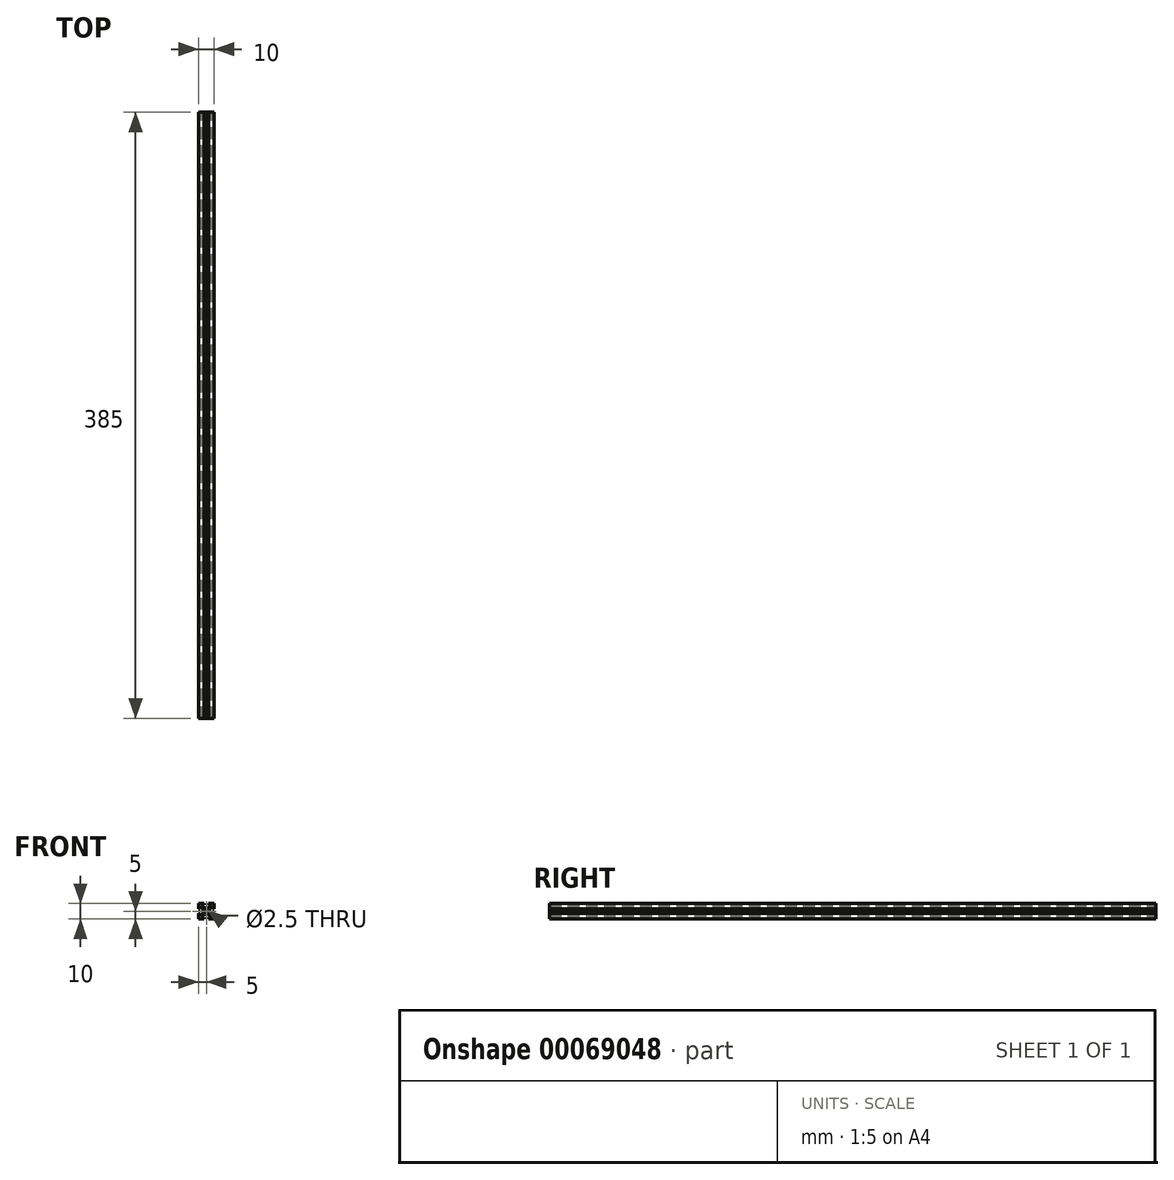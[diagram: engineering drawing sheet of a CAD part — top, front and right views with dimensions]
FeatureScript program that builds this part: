
annotation { "Feature Type Name" : "Feature", "Feature Type Description" : "" }
export const myFeature = defineFeature(function(context is Context, id is Id, definition is map)
    precondition{}
    {
        {
            var Q0;
            Q0=qCreatedBy(makeId("Front.planeOp"),FACE);
            var sketch = newSketch(context, id + "F0", { "sketchPlane" : qUnion([Q0])});
            skLineSegment(sketch, "E0", {"start": v(0, 0) * mm, "end": v(0, 3.5) * mm});
            skLineSegment(sketch, "E1", {"start": v(0, 3.5) * mm, "end": v(-1, 3.5) * mm});
            skLineSegment(sketch, "E2", {"start": v(-1, 3.5) * mm, "end": v(-1, 2) * mm});
            skLineSegment(sketch, "E3", {"start": v(-1, 2) * mm, "end": v(-3, 4) * mm});
            skLineSegment(sketch, "E4", {"start": v(-3, 4) * mm, "end": v(-3, 5) * mm});
            skLineSegment(sketch, "E5", {"start": v(-3, 5) * mm, "end": v(-5, 5) * mm, "construction": true});
            skLineSegment(sketch, "E6", {"start": v(-5, 5) * mm, "end": v(0, 0) * mm, "construction": true});
            skLineSegment(sketch, "E7.MirrorCS", {"start": v(-3.5, 0) * mm, "end": v(-3.5, 1) * mm});
            skLineSegment(sketch, "E8.MirrorCS", {"start": v(0, 0) * mm, "end": v(-3.5, 0) * mm});
            skLineSegment(sketch, "E9.MirrorCS", {"start": v(-3.5, 1) * mm, "end": v(-2, 1) * mm});
            skLineSegment(sketch, "E10.MirrorCS", {"start": v(-2, 1) * mm, "end": v(-4, 3) * mm});
            skLineSegment(sketch, "E11.MirrorCS", {"start": v(-4, 3) * mm, "end": v(-5, 3) * mm});
            skLineSegment(sketch, "E12.MirrorCS", {"start": v(-5, 3) * mm, "end": v(-5, 5) * mm, "construction": true});
            skLineSegment(sketch, "E13.1.0", {"start": v(-3, 6) * mm, "end": v(-3, 5) * mm});
            skLineSegment(sketch, "E13.1.1", {"start": v(-1, 8) * mm, "end": v(-3, 6) * mm});
            skLineSegment(sketch, "E13.1.2", {"start": v(-1, 6.5) * mm, "end": v(-1, 8) * mm});
            skLineSegment(sketch, "E13.1.3", {"start": v(0, 6.5) * mm, "end": v(-1, 6.5) * mm});
            skLineSegment(sketch, "E13.1.4", {"start": v(0, 10) * mm, "end": v(0, 6.5) * mm});
            skLineSegment(sketch, "E13.1.5", {"start": v(0, 10) * mm, "end": v(-3.5, 10) * mm});
            skLineSegment(sketch, "E13.1.6", {"start": v(-3.5, 10) * mm, "end": v(-3.5, 9) * mm});
            skLineSegment(sketch, "E13.1.7", {"start": v(-3.5, 9) * mm, "end": v(-2, 9) * mm});
            skLineSegment(sketch, "E13.1.8", {"start": v(-2, 9) * mm, "end": v(-4, 7) * mm});
            skLineSegment(sketch, "E13.1.9", {"start": v(-4, 7) * mm, "end": v(-5, 7) * mm});
            skLineSegment(sketch, "E13.2.0", {"start": v(-6, 7) * mm, "end": v(-5, 7) * mm});
            skLineSegment(sketch, "E13.2.1", {"start": v(-8, 9) * mm, "end": v(-6, 7) * mm});
            skLineSegment(sketch, "E13.2.2", {"start": v(-6.5, 9) * mm, "end": v(-8, 9) * mm});
            skLineSegment(sketch, "E13.2.3", {"start": v(-6.5, 10) * mm, "end": v(-6.5, 9) * mm});
            skLineSegment(sketch, "E13.2.4", {"start": v(-10, 10) * mm, "end": v(-6.5, 10) * mm});
            skLineSegment(sketch, "E13.2.5", {"start": v(-10, 10) * mm, "end": v(-10, 6.5) * mm});
            skLineSegment(sketch, "E13.2.6", {"start": v(-10, 6.5) * mm, "end": v(-9, 6.5) * mm});
            skLineSegment(sketch, "E13.2.7", {"start": v(-9, 6.5) * mm, "end": v(-9, 8) * mm});
            skLineSegment(sketch, "E13.2.8", {"start": v(-9, 8) * mm, "end": v(-7, 6) * mm});
            skLineSegment(sketch, "E13.2.9", {"start": v(-7, 6) * mm, "end": v(-7, 5) * mm});
            skLineSegment(sketch, "E13.3.0", {"start": v(-7, 4) * mm, "end": v(-7, 5) * mm});
            skLineSegment(sketch, "E13.3.1", {"start": v(-9, 2) * mm, "end": v(-7, 4) * mm});
            skLineSegment(sketch, "E13.3.2", {"start": v(-9, 3.5) * mm, "end": v(-9, 2) * mm});
            skLineSegment(sketch, "E13.3.3", {"start": v(-10, 3.5) * mm, "end": v(-9, 3.5) * mm});
            skLineSegment(sketch, "E13.3.4", {"start": v(-10, 0) * mm, "end": v(-10, 3.5) * mm});
            skLineSegment(sketch, "E13.3.5", {"start": v(-10, 0) * mm, "end": v(-6.5, 0) * mm});
            skLineSegment(sketch, "E13.3.6", {"start": v(-6.5, 0) * mm, "end": v(-6.5, 1) * mm});
            skLineSegment(sketch, "E13.3.7", {"start": v(-6.5, 1) * mm, "end": v(-8, 1) * mm});
            skLineSegment(sketch, "E13.3.8", {"start": v(-8, 1) * mm, "end": v(-6, 3) * mm});
            skLineSegment(sketch, "E13.3.9", {"start": v(-6, 3) * mm, "end": v(-5, 3) * mm});
            skPoint(sketch, "E13.center", {"position": v(-5, 5) * mm});
            skCircle(sketch, "E14", {"center": v(-5, 5) * mm, "radius": 1.25 * mm});
            skSolve(sketch);
        }
        {
            var Q0;
            Q0=makeQuery(id+"F0.imprint","IMPRINT",FACE,{"disambiguationData":[TD([[makeQuery(id+"F0.imprint","IMPRINT",EDGE,{"derivedFrom":sQuery(id+"F0.wireOp",EDGE,"E0")}),1.0]])]});
            extrude(context, id + "F1", {"entities" : qUnion([Q0]), "depth" : 385 * mm});
        }
    });
